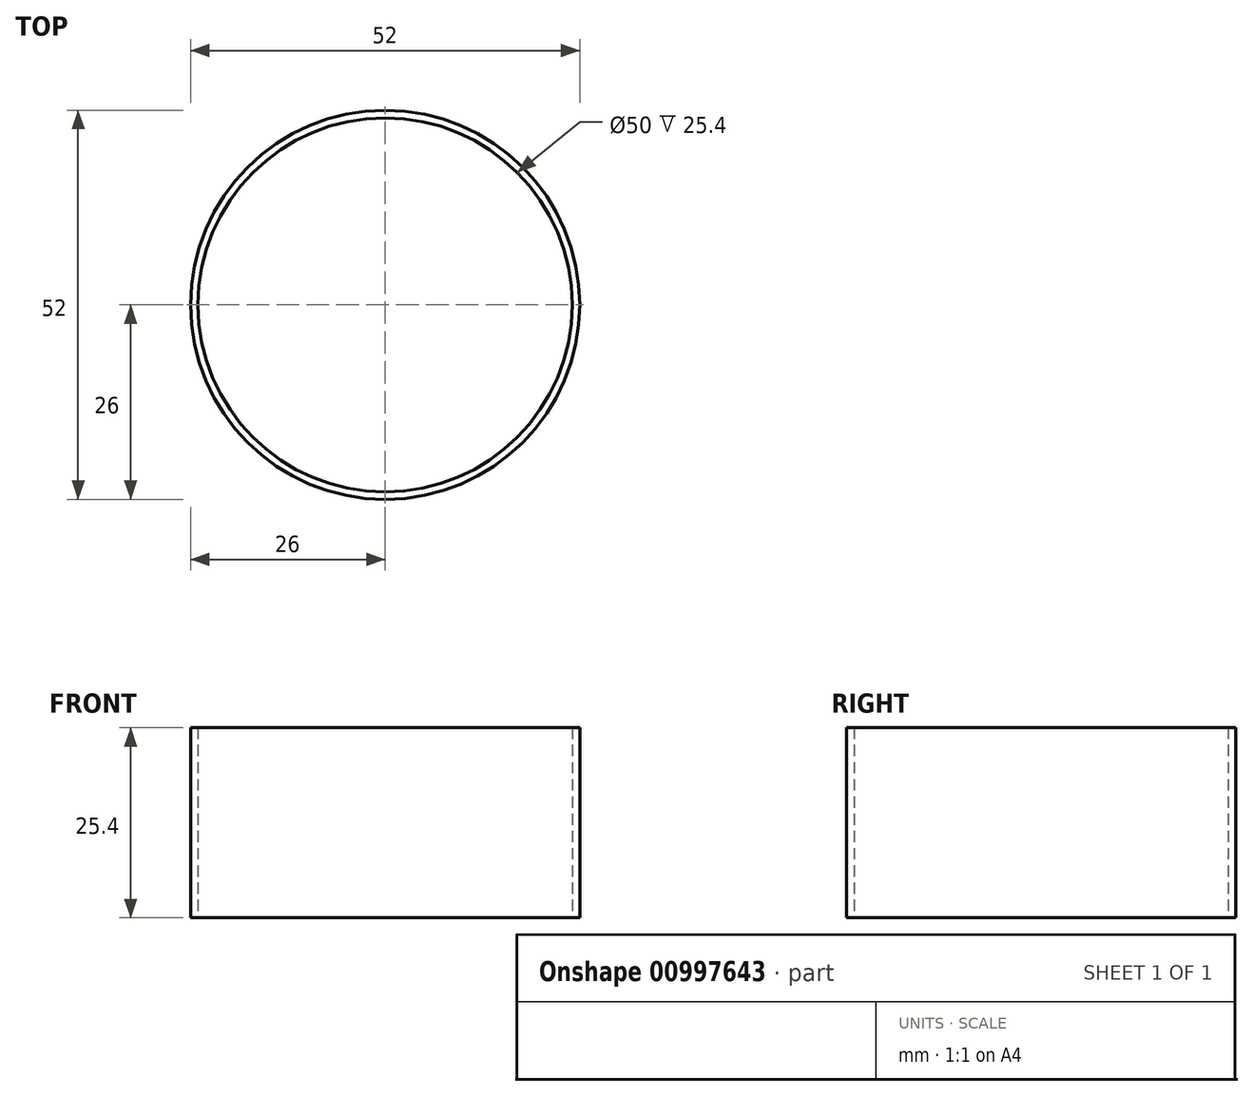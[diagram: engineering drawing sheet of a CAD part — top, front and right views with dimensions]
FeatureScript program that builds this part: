
annotation { "Feature Type Name" : "Feature", "Feature Type Description" : "" }
export const myFeature = defineFeature(function(context is Context, id is Id, definition is map)
    precondition{}
    {
        {
            var Q0;
            Q0=qCreatedBy(makeId("Top.planeOp"),FACE);
            var sketch = newSketch(context, id + "F0", { "sketchPlane" : qUnion([Q0])});
            skCircle(sketch, "E0", {"center": v(0, 0) * mm, "radius": 26 * mm});
            skCircle(sketch, "E1", {"center": v(0, 0) * mm, "radius": 25 * mm});
            skSolve(sketch);
        }
        {
            var Q0;
            Q0 = qSketchRegion(id + "F0", true);
            extrude(context, id + "F1", {"entities" : qUnion([Q0]), "depth" : 25.4 * mm, "offsetDistance" : 25.4 * mm});
        }
    });
